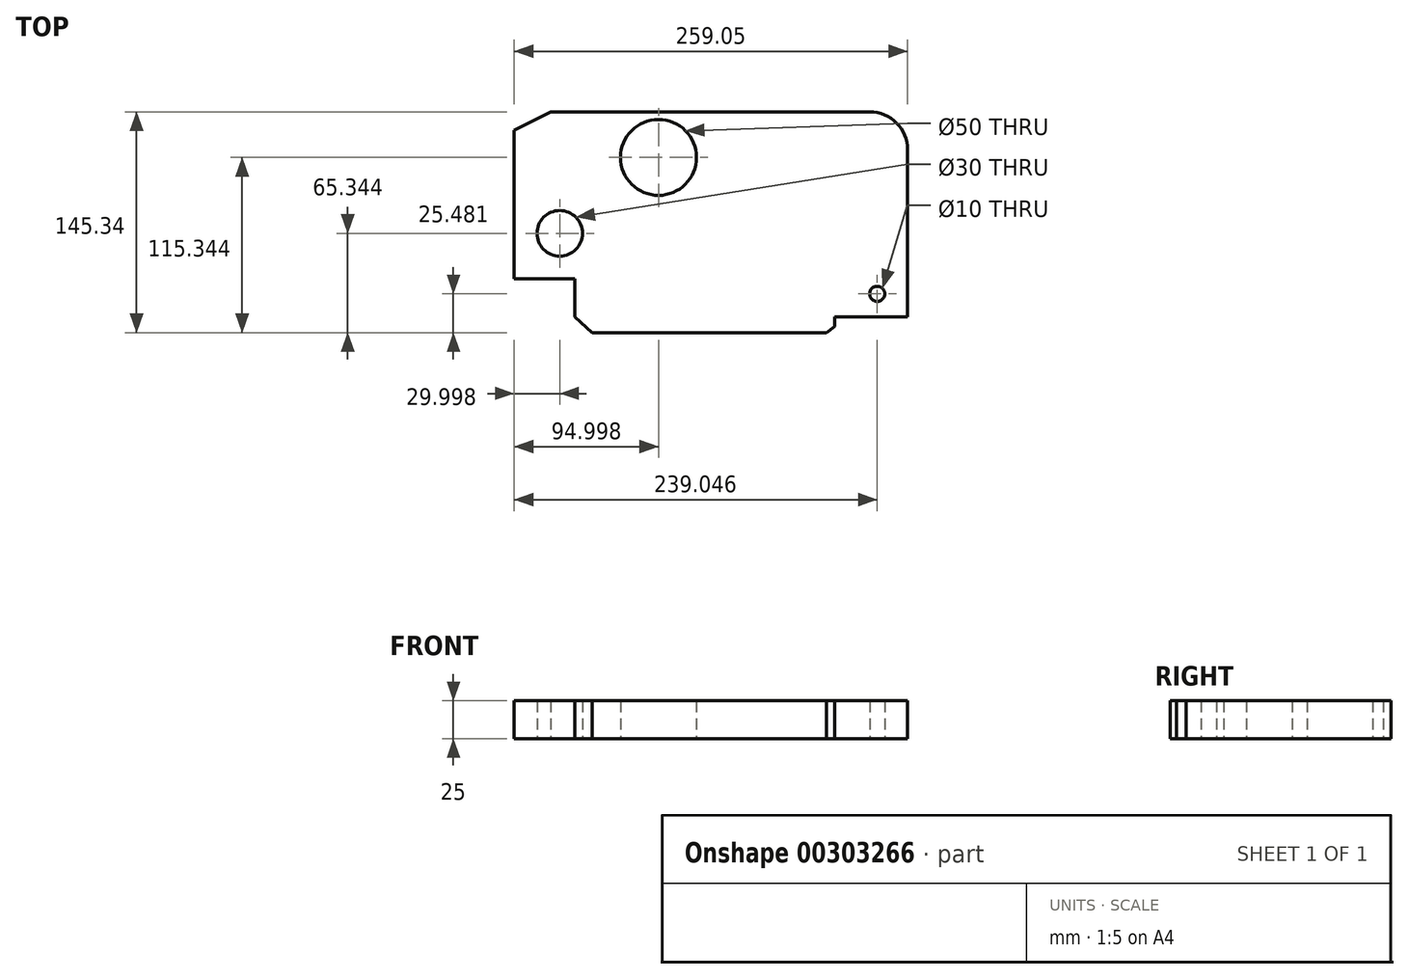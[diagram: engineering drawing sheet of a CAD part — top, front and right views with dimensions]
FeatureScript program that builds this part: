
annotation { "Feature Type Name" : "Feature", "Feature Type Description" : "" }
export const myFeature = defineFeature(function(context is Context, id is Id, definition is map)
    precondition{}
    {
        {
            var Q0;
            Q0=qCreatedBy(makeId("Top.planeOp"),FACE);
            var sketch = newSketch(context, id + "F0", { "sketchPlane" : qUnion([Q0])});
            skLineSegment(sketch, "E0", {"start": v(-83.91, 47.33) * mm, "end": v(71.33, 47.33) * mm});
            skLineSegment(sketch, "E1", {"start": v(-83.91, 47.33) * mm, "end": v(-107.91, 35.33) * mm});
            skLineSegment(sketch, "E2", {"start": v(-107.91, 35.33) * mm, "end": v(-107.91, -62.67) * mm});
            skLineSegment(sketch, "E3", {"start": v(-107.91, -62.67) * mm, "end": v(-67.91, -62.67) * mm});
            skLineSegment(sketch, "E4", {"start": v(-67.91, -62.67) * mm, "end": v(-67.91, -87.53) * mm});
            skLineSegment(sketch, "E5", {"start": v(-67.91, -87.53) * mm, "end": v(-56.48, -98) * mm});
            skLineSegment(sketch, "E6", {"start": v(-56.48, -98) * mm, "end": v(97.8, -98) * mm});
            skLineSegment(sketch, "E7", {"start": v(151.14, -87.53) * mm, "end": v(151.14, 22.33) * mm});
            skLineSegment(sketch, "E8", {"start": v(126.14, 47.33) * mm, "end": v(71.33, 47.33) * mm});
            skLineSegment(sketch, "E9", {"start": v(-107.91, -62.67) * mm, "end": v(-107.91, -32.67) * mm});
            skCircle(sketch, "E10", {"center": v(-77.91, -32.67) * mm, "radius": 15 * mm});
            skLineSegment(sketch, "E11", {"start": v(-83.91, 47.33) * mm, "end": v(-12.91, 47.33) * mm});
            skCircle(sketch, "E12", {"center": v(-12.91, 17.33) * mm, "radius": 25 * mm});
            skCircle(sketch, "E13", {"center": v(131.14, -72.53) * mm, "radius": 5 * mm});
            skPoint(sketch, "E14.visualSharp", {"position": v(151.14, 47.33) * mm});
            skArc(sketch, "E14.filletArc", {"start": v(151.14, 22.33) * mm, "mid": v(143.81, 40.01) * mm, "end": v(126.14, 47.33) * mm});
            skPoint(sketch, "E15.end.orphan", {"position": v(131.14, -87.53) * mm});
            skPoint(sketch, "E16.end.orphan", {"position": v(111.14, -87.53) * mm});
            skLineSegment(sketch, "E17", {"start": v(97.8, -98) * mm, "end": v(103.08, -93.9) * mm});
            skLineSegment(sketch, "E18", {"start": v(103.08, -93.9) * mm, "end": v(103.08, -87.53) * mm});
            skLineSegment(sketch, "E19", {"start": v(103.08, -87.53) * mm, "end": v(151.14, -87.53) * mm});
            skSolve(sketch);
        }
        {
            var Q0;
            Q0 = qSketchRegion(id + "F0", true);
            extrude(context, id + "F1", {"entities" : qUnion([Q0]), "depth" : 25 * mm});
        }
    });
